# Revit family: Plumbing-Flushometer-Sloan-Valve-ROYAL-180-ESSz
name_source: partatom
category: Plumbing Fixtures
units: mm (PartAtom-declared; Revit-internal decimal feet)

## family parameters
Cut with Voids When Loaded = No
Host = Face
OmniClass Number = 23.45.05.14.99
OmniClass Title = Other Sanitary Washing Plumbing Fixtures
Part Type = Normal
Room Calculation Point = No
Round Connector Dimension = Use Diameter
Shared = No

## types (9) — shared parameters
Apparent Load = 0 VA
Assembly Code = D2020300
CW Connection = Yes
Centerline of Supply from Top of Fixture = 11 1/2"
Centerline of Supply to Centerline of Valve = 4 3/4"
Current = 0 A
Default Elevation = 0"
Edition number = 1
HW Connection = No
Height = 13 5/8"
Keynote = 15410
Manufacturer = Sloan Valve
Number of Poles = 3
Operating Water Pressure = 15 – 80 PSI (103 – 552 kPa)
Power Factor = 0.8
Product Material = Sloan Valve - Finish - Polished Chrome
Product data url = https://bimobject.com
URL = www.sloanvalve.com
Valve Pressure Drop = 0.00 psi
Vent Connection = No
Voltage = 24 V
Waste Connection = No
Water Inlet Connection Diameter = 1"
z_Electrical Box = Yes
zero-valued in all types: CWFU, HWFU, WFU

## per-type parameters (varying)
| type | Description | Flush Rate | Part Number |
| ROYAL 180 ESS-1.0-TMO-HW | 1.0 gpf, Polished Chrome Finish, Fixture Connection Top Spud, Single Flush, True Mechanical Override, Hardwired, Sensor-Operated, Royal® Exposed Sensor Hardwired Urinal Flushometer. | 1.0 gpf (3.8 Lpf) | 3452430 |
| ROYAL 180 ESS-1.0-HW | 1.0 gpf, Polished Chrome Finish, Fixture Connection Top Spud, Single Flush, Hardwired, Sensor-Operated, Royal® Exposed Sensor Hardwired Urinal Flushometer. | 1.0 gpf (3.8 Lpf) | 3452473 |
| ROYAL 180 ESS-1.5-HW | 1.5 gpf, Polished Chrome Finish, Fixture Connection Top Spud, Single Flush, Hardwired, Sensor-Operated, Royal® Exposed Sensor Hardwired Urinal Flushometer. | 1.5 gpf (5.7 Lpf) | 3452449 |
| ROYAL 180 ESS-3.5-OR-HW | 3.5 gpf, Polished Chrome Finish, Fixture Connection Top Spud, Single Flush, Electrical Override, Hardwired, Sensor-Operated, Royal® Exposed Sensor Hardwired Urinal Flushometer. | 3.5 gpf (13.2 Lpf) | 3452447 |
| ROYAL 180 ESS-1.5-TMO-HW | 1.5 gpf, Polished Chrome Finish, Fixture Connection Top Spud, Single Flush, True Mechanical Override, Hardwired, Sensor-Operated, Royal® Exposed Sensor Hardwired Urinal Flushometer. | 1.5 gpf (5.7 Lpf) | 3452435 |
| ROYAL 180 ESS-1.0-GJ-HW | 1.0 gpf, Polished Chrome Finish, Fixture Connection Top Spud, Single Flush, Ground Joint Control Stop, Hardwired, Sensor-Operated, Royal® Exposed Sensor Hardwired Urinal Flushometer. | 1.0 gpf (3.8 Lpf) | 3452413 |
| ROYAL 180 ESS-1.5-T-HW | 1.5 gpf, Polished Chrome Finish, 1.5" Flush Connection, Fixture Connection Top Spud, Single Flush, Hardwired, Sensor-Operated, Royal® Exposed Sensor Hardwired Urinal Flushometer. | 1.5 gpf (5.7 Lpf) | 3452402 |
| ROYAL 180 ESS-3.5-T-OR-HW | 3.5 gpf, Polished Chrome Finish, 1.5" Flush Connection, Fixture Connection Top Spud, Single Flush, Electrical Override, Hardwired, Sensor-Operated, Royal® Exposed Sensor Hardwired Urinal Flushometer. | 3.5 gpf (13.2 Lpf) | 3912492 |
| ROYAL 180 ESS-3.5-T-OR-RGL-PLT-HW | 3.5 gpf, Polished Chrome Finish, 1.5" Flush Connection, Fixture Connection Top Spud, Single Flush, Electrical Override, Hardwired, Sensor-Operated, Regal Plate Wall Box, Royal® Exposed Sensor Hardwired Urinal Flushometer. | 3.5 gpf (13.2 Lpf) | 3452401 |

note: column(s) folded — value = type name in every type: Model

## geometry (parser evidence)
native form markers: Sweep x6
no freeform markers — native parametric forms only
